# Revit family: Safety-Equipment_Fences-Gates_Omega-Industrial_Hand-Rail-Swing-Gate
name_source: partatom
category: Generic Models
units: mm (PartAtom-declared; Revit-internal decimal feet)

## family parameters
Always vertical = Yes
Can host rebar = No
Classification Number = 23.30.80.17
Cut with Voids When Loaded = No
Maintain Annotation Orientation = No
Part Type = Normal
Room Calculation Point = No
Round Connector Dimension = Use Diameter
Shared = No
Work Plane-Based = Yes

## types (2) — shared parameters
Assembly Code = E1090
Default Elevation = 3' - 6"
Expected Lifespan (Years) = 25
Installation Phase = Industrial Safety Equipment
Keynote = 41 67 19
Manufacturer = Omega Industrial Products, Inc.
Manufacturer Fax = 262-284-4199
Manufacturer Website = https://www.omegaindl.com
Pipe Diameter = 0' - 1 1/2"
Pipe Material = Omega_7 Ga. Steel
Pipe Radius = 0' - 0 3/4"
Product Data = https://www.arcat.com
Product Properties = https://www.omegaindl.com
Revision = R0_06-2018
Sales Information = https://www.omegaindl.com
Send Message = https://www.omegaindl.com
Specification = https://www.arcat.com
URL = https://www.arcat.com
Unit Depth = 0' - 10"
Unit Height = 2' - 0"
zero-valued in all types: Maintenance Schedule (Months), Warranty Duration (Years)

## per-type parameters (varying)
| type | Description | Model | Unit Width |
| 36in. x 24in. | 48 inch Handrail Swing Gate | HR-GS-2-HD-48 | 3' - 0" |
| 48in. x 24in. | 36 inch Handrail Swing Gate | HR-GS2-PIPE | 4' - 0" |

## geometry (parser evidence)
native form markers: Blend x40, Sweep x1
no freeform markers — native parametric forms only
